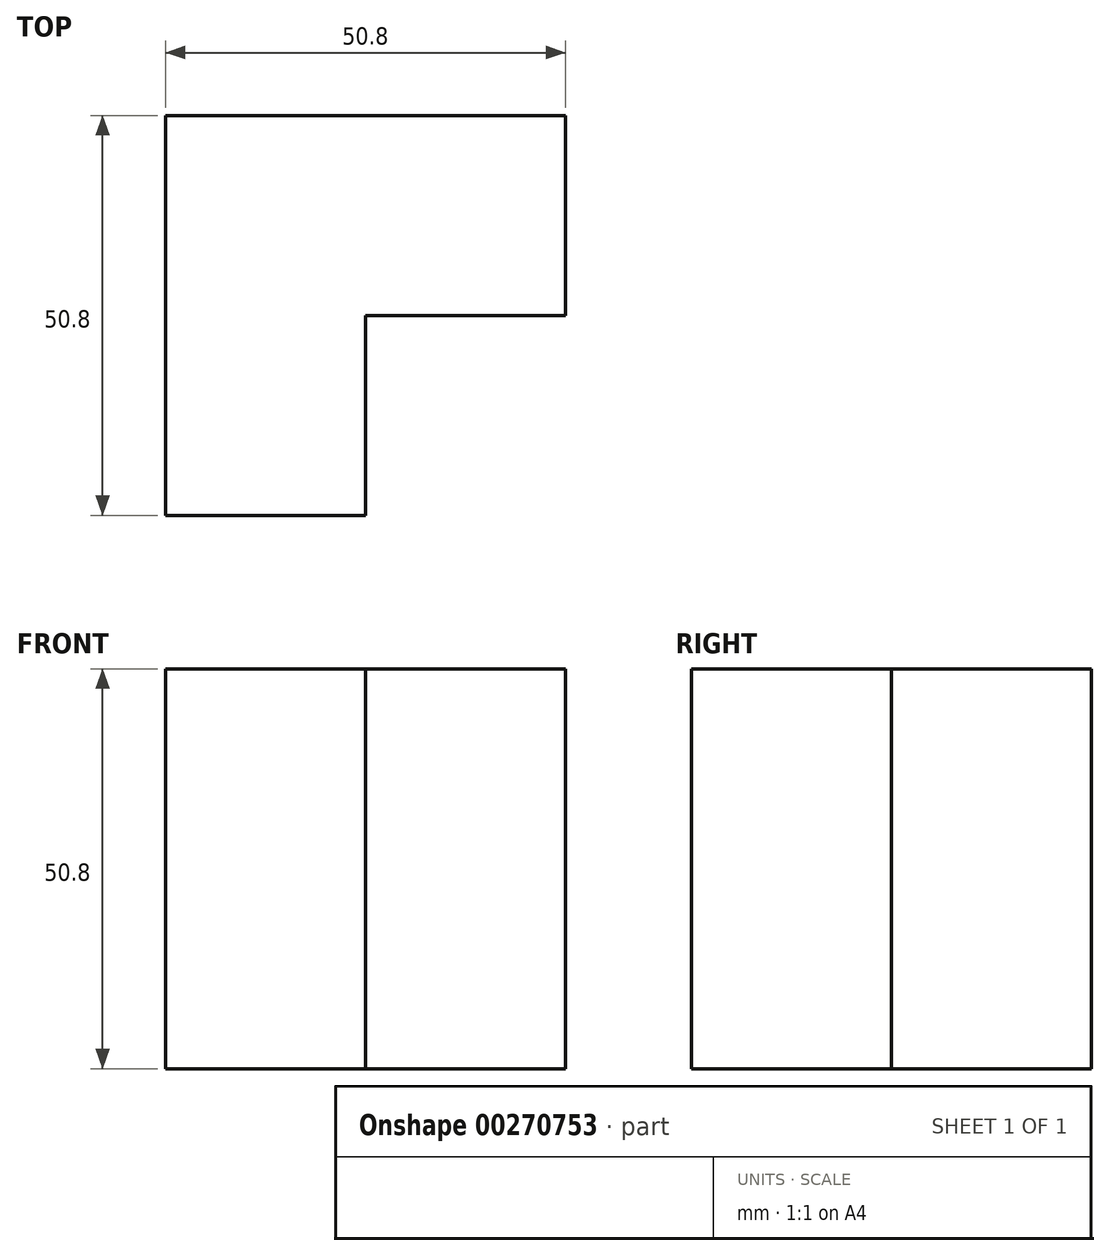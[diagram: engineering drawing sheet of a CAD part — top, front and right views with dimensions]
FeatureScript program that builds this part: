
annotation { "Feature Type Name" : "Feature", "Feature Type Description" : "" }
export const myFeature = defineFeature(function(context is Context, id is Id, definition is map)
    precondition{}
    {
        {
            var Q0;
            Q0=qCreatedBy(makeId("Front.planeOp"),FACE);
            var sketch = newSketch(context, id + "F0", { "sketchPlane" : qUnion([Q0])});
            skLineSegment(sketch, "E0.bottom", {"start": v(0, 0) * mm, "end": v(-50.8, 0) * mm});
            skLineSegment(sketch, "E0.top", {"start": v(0, 50.8) * mm, "end": v(-50.8, 50.8) * mm});
            skLineSegment(sketch, "E0.left", {"start": v(0, 0) * mm, "end": v(0, 50.8) * mm});
            skLineSegment(sketch, "E0.right", {"start": v(-50.8, 0) * mm, "end": v(-50.8, 50.8) * mm});
            skSolve(sketch);
        }
        {
            var Q0;
            Q0=makeQuery(id+"F0.imprint","IMPRINT",FACE,{"disambiguationData":[TD([[makeQuery(id+"F0.imprint","IMPRINT",EDGE,{"derivedFrom":sQuery(id+"F0.wireOp",EDGE,"E0.bottom")}),-1.0]])]});
            extrude(context, id + "F1", {"entities" : qUnion([Q0]), "depth" : 50.8 * mm});
        }
        {
            var Q0;
            Q0=makeQuery(id+"F1.opExtrude","CAP_FACE",FACE,{"disambiguationData":[OSD([sQuery(id+"F0.wireOp",EDGE,"E0.bottom"),sQuery(id+"F0.wireOp",EDGE,"E0.top"),sQuery(id+"F0.wireOp",EDGE,"E0.left"),sQuery(id+"F0.wireOp",EDGE,"E0.right")])],"isStart":false});
            var sketch = newSketch(context, id + "F2", { "sketchPlane" : qUnion([Q0])});
            skLineSegment(sketch, "E1", {"start": v(0, 50.8) * mm, "end": v(-25.4, 50.8) * mm});
            skLineSegment(sketch, "E2", {"start": v(-25.4, 50.8) * mm, "end": v(-25.4, 0) * mm});
            skLineSegment(sketch, "E3", {"start": v(-25.4, 0) * mm, "end": v(0, 0) * mm});
            skLineSegment(sketch, "E4", {"start": v(0, 0) * mm, "end": v(0, 50.8) * mm});
            skSolve(sketch);
        }
        {
            var Q0;
            Q0=makeQuery(id+"F2.imprint","IMPRINT",FACE,{"disambiguationData":[TD([[makeQuery(id+"F2.imprint","IMPRINT",EDGE,{"derivedFrom":sQuery(id+"F2.wireOp",EDGE,"E1")}),1.0]])]});
            extrude(context, id + "F3", {"entities" : qUnion([Q0]), "operationType" : NewBodyOperationType.REMOVE, "oppositeDirection" : true, "depth" : 25.4 * mm});
        }
    });
